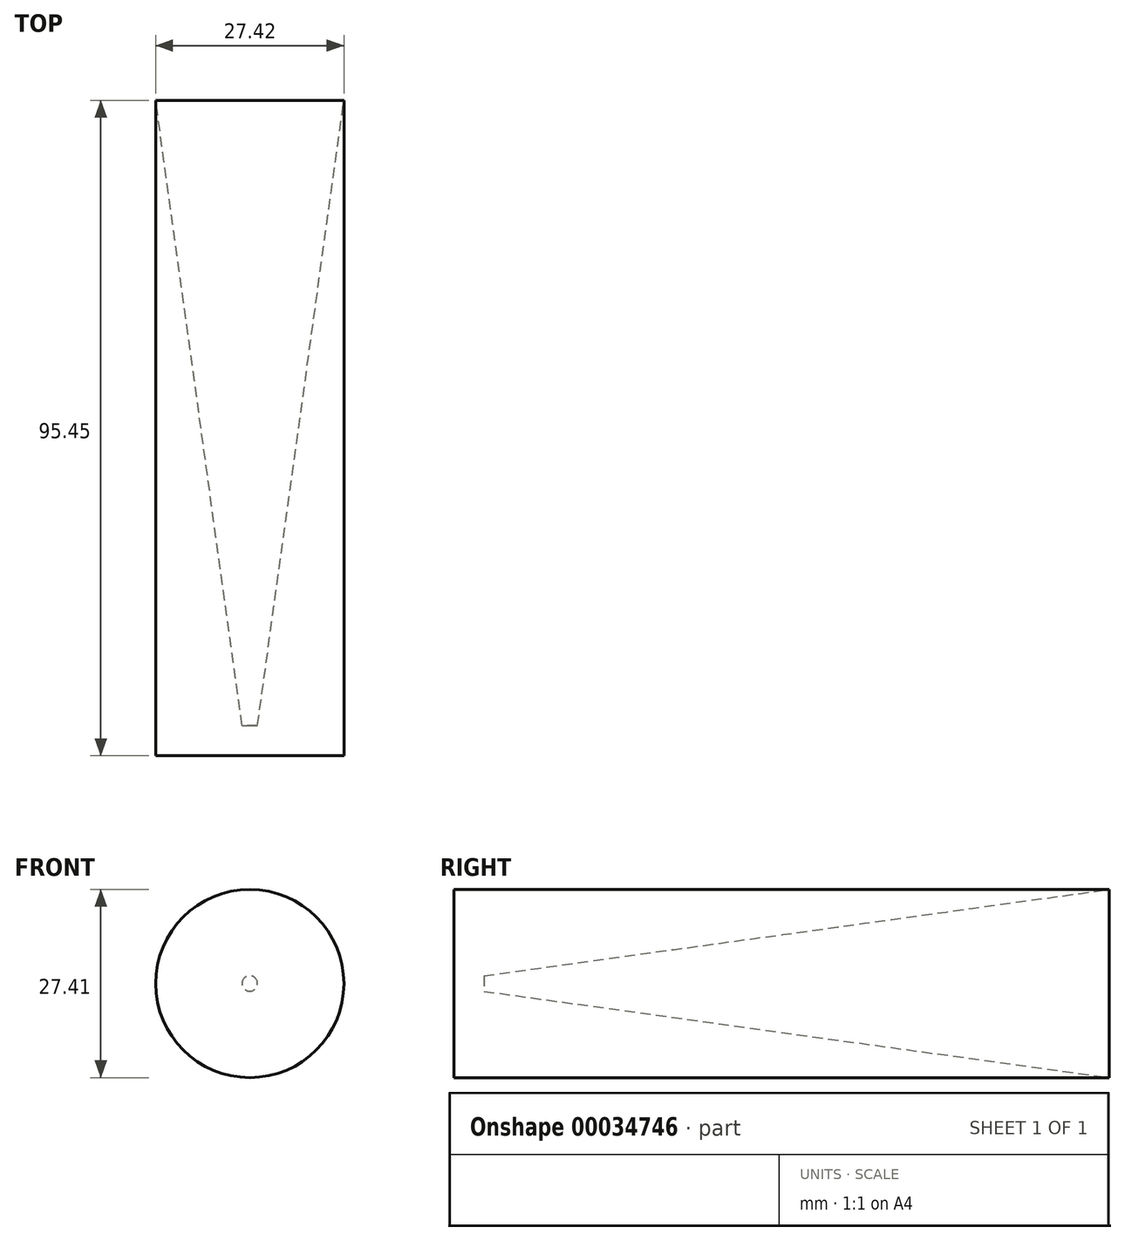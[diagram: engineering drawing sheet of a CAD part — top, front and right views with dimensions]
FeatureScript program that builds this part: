
annotation { "Feature Type Name" : "Feature", "Feature Type Description" : "" }
export const myFeature = defineFeature(function(context is Context, id is Id, definition is map)
    precondition{}
    {
        {
            var Q0;
            Q0=qCreatedBy(makeId("Right.planeOp"),FACE);
            var sketch = newSketch(context, id + "F0", { "sketchPlane" : qUnion([Q0])});
            skLineSegment(sketch, "E0", {"start": v(-67.34, -0.05) * mm, "end": v(-71.74, -0.05) * mm});
            skLineSegment(sketch, "E1", {"start": v(-71.74, -0.05) * mm, "end": v(-71.74, 13.65) * mm});
            skLineSegment(sketch, "E2", {"start": v(-71.74, 13.65) * mm, "end": v(23.71, 13.65) * mm});
            skLineSegment(sketch, "E3", {"start": v(23.71, 13.65) * mm, "end": v(-67.34, 1.07) * mm});
            skLineSegment(sketch, "E4", {"start": v(-67.34, 1.07) * mm, "end": v(-67.34, -0.05) * mm});
            skSolve(sketch);
        }
        {
            var Q0;
            Q0=makeQuery(id+"F0.imprint","IMPRINT",FACE,{"disambiguationData":[TD([[makeQuery(id+"F0.imprint","IMPRINT",EDGE,{"derivedFrom":sQuery(id+"F0.wireOp",EDGE,"E0")}),-1.0]])]});
            var Q1;
            Q1=sQuery(id+"F0.wireOp",EDGE,"E1");
            var Q2;
            Q2=sQuery(id+"F0.wireOp",EDGE,"E2");
            var Q3;
            Q3=sQuery(id+"F0.wireOp",EDGE,"E3");
            var Q4;
            Q4=sQuery(id+"F0.wireOp",EDGE,"E3");
            var Q5;
            Q5=sQuery(id+"F0.wireOp",EDGE,"E2");
            var Q6;
            Q6=sQuery(id+"F0.wireOp",EDGE,"E1");
            var Q7;
            Q7=sQuery(id+"F0.wireOp",EDGE,"E0");
            var Q8;
            Q8=sQuery(id+"F0.wireOp",EDGE,"E4");
            var Q9;
            Q9=sQuery(id+"F0.wireOp",EDGE,"E4");
            var Q10;
            Q10=sQuery(id+"F0.wireOp",EDGE,"E0");
            var Q11;
            Q11=sQuery(id+"F0.wireOp",EDGE,"E0");
            revolve(context, id + "F1", {"entities" : qUnion([Q0]), "surfaceEntities" : qUnion([Q1, Q2, Q3, Q4, Q5, Q6, Q7, Q8, Q9, Q10]), "axis" : qUnion([Q11]), "revolveType" : RevolveType.FULL});
        }
    });
